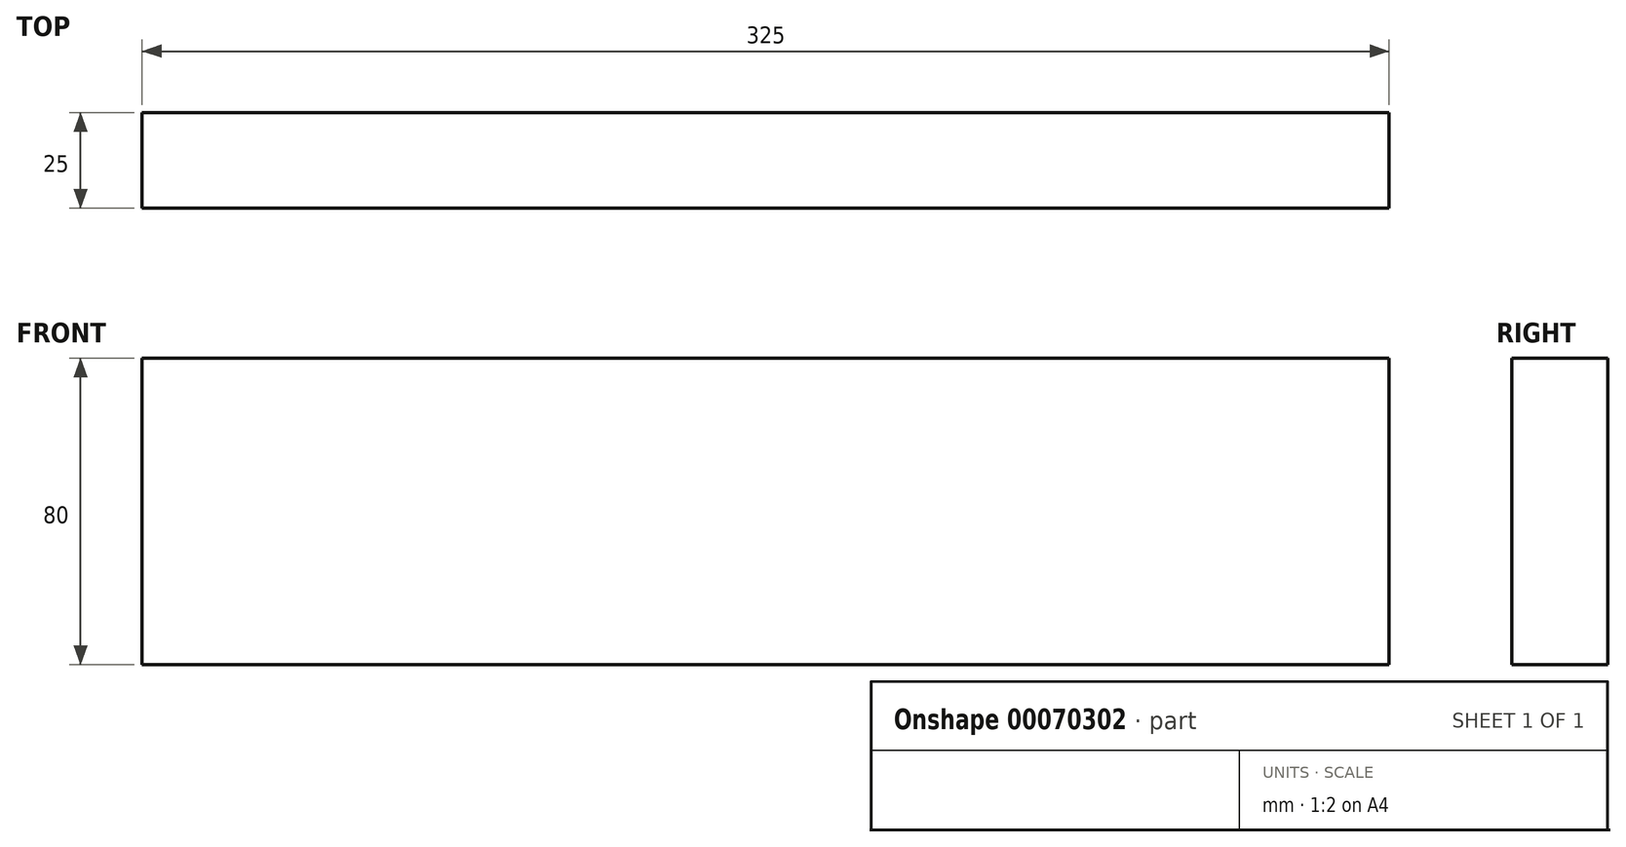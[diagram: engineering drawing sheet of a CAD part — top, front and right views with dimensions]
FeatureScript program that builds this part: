
annotation { "Feature Type Name" : "Feature", "Feature Type Description" : "" }
export const myFeature = defineFeature(function(context is Context, id is Id, definition is map)
    precondition{}
    {
        {
            var Q0;
            Q0=qCreatedBy(makeId("Front.planeOp"),FACE);
            var sketch = newSketch(context, id + "F0", { "sketchPlane" : qUnion([Q0])});
            skLineSegment(sketch, "E0.bottom", {"start": v(-229.85, 0) * mm, "end": v(95.15, 0) * mm});
            skLineSegment(sketch, "E0.top", {"start": v(-229.85, -80) * mm, "end": v(95.15, -80) * mm});
            skLineSegment(sketch, "E0.left", {"start": v(-229.85, 0) * mm, "end": v(-229.85, -80) * mm});
            skLineSegment(sketch, "E0.right", {"start": v(95.15, 0) * mm, "end": v(95.15, -80) * mm});
            skLineSegment(sketch, "E1.bottom", {"start": v(-154.85, 0) * mm, "end": v(20.15, 0) * mm});
            skLineSegment(sketch, "E1.top", {"start": v(-154.85, 75) * mm, "end": v(20.15, 75) * mm});
            skLineSegment(sketch, "E1.left", {"start": v(-154.85, 0) * mm, "end": v(-154.85, 75) * mm});
            skLineSegment(sketch, "E1.right", {"start": v(20.15, 0) * mm, "end": v(20.15, 75) * mm});
            skSolve(sketch);
        }
        {
            var Q0;
            Q0=makeQuery(id+"F0.imprint","IMPRINT",FACE,{"disambiguationData":[TD([[makeQuery(id+"F0.imprint","IMPRINT",EDGE,{"derivedFrom":sQuery(id+"F0.wireOp",EDGE,"E1.bottom")}),1.0]])]});
            var Q1;
            Q1=makeQuery(id+"F0.imprint","IMPRINT",FACE,{"disambiguationData":[TD([[makeQuery(id+"F0.imprint","IMPRINT",EDGE,{"derivedFrom":sQuery(id+"F0.wireOp",EDGE,"E0.top")}),1.0]])]});
            extrude(context, id + "F1", {"entities" : qUnion([Q0, Q1]), "depth" : 25 * mm});
        }
    });
